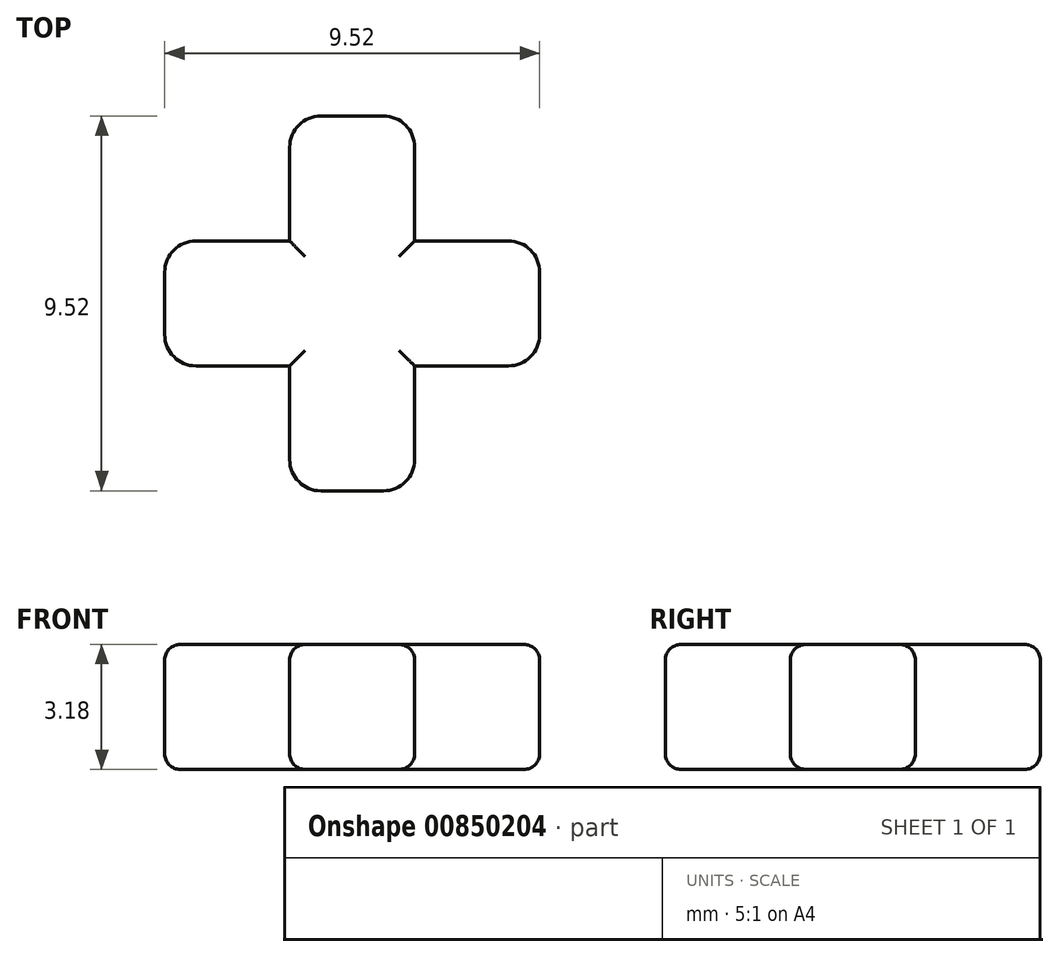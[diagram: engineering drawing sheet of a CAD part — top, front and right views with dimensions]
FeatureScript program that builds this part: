
annotation { "Feature Type Name" : "Feature", "Feature Type Description" : "" }
export const myFeature = defineFeature(function(context is Context, id is Id, definition is map)
    precondition{}
    {
        {
            var Q0;
            Q0=qCreatedBy(makeId("Top.planeOp"),FACE);
            var sketch = newSketch(context, id + "F0", { "sketchPlane" : qUnion([Q0])});
            skLineSegment(sketch, "E0.bottom", {"start": v(0.8, 4.76) * mm, "end": v(-0.8, 4.76) * mm});
            skLineSegment(sketch, "E0.top", {"start": v(0.8, -4.76) * mm, "end": v(-0.8, -4.76) * mm});
            skLineSegment(sketch, "E0.left", {"start": v(1.59, 3.97) * mm, "end": v(1.59, -3.97) * mm});
            skLineSegment(sketch, "E0.right", {"start": v(-1.59, 3.97) * mm, "end": v(-1.59, -3.97) * mm});
            skPoint(sketch, "E0.middle", {"position": v(0, 0) * mm});
            skLineSegment(sketch, "E1.bottom", {"start": v(3.97, 1.59) * mm, "end": v(-3.97, 1.59) * mm});
            skLineSegment(sketch, "E1.top", {"start": v(3.97, -1.59) * mm, "end": v(-3.97, -1.59) * mm});
            skLineSegment(sketch, "E1.left", {"start": v(4.76, 0.8) * mm, "end": v(4.76, -0.8) * mm});
            skLineSegment(sketch, "E1.right", {"start": v(-4.76, 0.8) * mm, "end": v(-4.76, -0.8) * mm});
            skPoint(sketch, "E2.visualSharp", {"position": v(-1.59, 4.76) * mm});
            skArc(sketch, "E2.filletArc", {"start": v(-0.8, 4.76) * mm, "mid": v(-1.36, 4.53) * mm, "end": v(-1.59, 3.97) * mm});
            skPoint(sketch, "E3.visualSharp", {"position": v(1.59, 4.76) * mm});
            skArc(sketch, "E3.filletArc", {"start": v(1.59, 3.97) * mm, "mid": v(1.36, 4.53) * mm, "end": v(0.8, 4.76) * mm});
            skPoint(sketch, "E4.visualSharp", {"position": v(4.76, 1.59) * mm});
            skArc(sketch, "E4.filletArc", {"start": v(4.76, 0.8) * mm, "mid": v(4.53, 1.36) * mm, "end": v(3.97, 1.59) * mm});
            skPoint(sketch, "E5.visualSharp", {"position": v(4.76, -1.59) * mm});
            skArc(sketch, "E5.filletArc", {"start": v(3.97, -1.59) * mm, "mid": v(4.53, -1.36) * mm, "end": v(4.76, -0.8) * mm});
            skPoint(sketch, "E6.visualSharp", {"position": v(1.59, -4.76) * mm});
            skArc(sketch, "E6.filletArc", {"start": v(0.8, -4.76) * mm, "mid": v(1.36, -4.53) * mm, "end": v(1.59, -3.97) * mm});
            skPoint(sketch, "E7.visualSharp", {"position": v(-1.59, -4.76) * mm});
            skArc(sketch, "E7.filletArc", {"start": v(-1.59, -3.97) * mm, "mid": v(-1.36, -4.53) * mm, "end": v(-0.8, -4.76) * mm});
            skPoint(sketch, "E8.visualSharp", {"position": v(-4.76, -1.59) * mm});
            skArc(sketch, "E8.filletArc", {"start": v(-4.76, -0.8) * mm, "mid": v(-4.53, -1.36) * mm, "end": v(-3.97, -1.59) * mm});
            skPoint(sketch, "E9.visualSharp", {"position": v(-4.76, 1.59) * mm});
            skArc(sketch, "E9.filletArc", {"start": v(-3.97, 1.59) * mm, "mid": v(-4.53, 1.36) * mm, "end": v(-4.76, 0.8) * mm});
            skSolve(sketch);
        }
        {
            var Q0;
            Q0 = qSketchRegion(id + "F0", true);
            extrude(context, id + "F1", {"entities" : qUnion([Q0]), "depth" : 3.17 * mm, "offsetDistance" : 25.4 * mm});
        }
        {
            var Q0;
            Q0=makeQuery(id+"F1.opExtrude","CAP_FACE",FACE,{"disambiguationData":[OSD([sQuery(id+"F0.wireOp",EDGE,"E0.bottom"),sQuery(id+"F0.wireOp",EDGE,"E0.top"),sQuery(id+"F0.wireOp",EDGE,"E0.left"),sQuery(id+"F0.wireOp",EDGE,"E0.right"),sQuery(id+"F0.wireOp",EDGE,"E1.bottom"),sQuery(id+"F0.wireOp",EDGE,"E1.top"),sQuery(id+"F0.wireOp",EDGE,"E1.left"),sQuery(id+"F0.wireOp",EDGE,"E1.right"),sQuery(id+"F0.wireOp",EDGE,"E2.filletArc"),sQuery(id+"F0.wireOp",EDGE,"E3.filletArc"),sQuery(id+"F0.wireOp",EDGE,"E4.filletArc"),sQuery(id+"F0.wireOp",EDGE,"E5.filletArc"),sQuery(id+"F0.wireOp",EDGE,"E6.filletArc"),sQuery(id+"F0.wireOp",EDGE,"E7.filletArc"),sQuery(id+"F0.wireOp",EDGE,"E8.filletArc"),sQuery(id+"F0.wireOp",EDGE,"E9.filletArc")])],"isStart":false});
            var Q1;
            Q1=makeQuery(id+"F1.opExtrude","CAP_FACE",FACE,{"disambiguationData":[OSD([sQuery(id+"F0.wireOp",EDGE,"E0.bottom"),sQuery(id+"F0.wireOp",EDGE,"E0.top"),sQuery(id+"F0.wireOp",EDGE,"E0.left"),sQuery(id+"F0.wireOp",EDGE,"E0.right"),sQuery(id+"F0.wireOp",EDGE,"E1.bottom"),sQuery(id+"F0.wireOp",EDGE,"E1.top"),sQuery(id+"F0.wireOp",EDGE,"E1.left"),sQuery(id+"F0.wireOp",EDGE,"E1.right"),sQuery(id+"F0.wireOp",EDGE,"E2.filletArc"),sQuery(id+"F0.wireOp",EDGE,"E3.filletArc"),sQuery(id+"F0.wireOp",EDGE,"E4.filletArc"),sQuery(id+"F0.wireOp",EDGE,"E5.filletArc"),sQuery(id+"F0.wireOp",EDGE,"E6.filletArc"),sQuery(id+"F0.wireOp",EDGE,"E7.filletArc"),sQuery(id+"F0.wireOp",EDGE,"E8.filletArc"),sQuery(id+"F0.wireOp",EDGE,"E9.filletArc")])],"isStart":true});
            fillet(context, id + "F2", {"entities" : qUnion([Q0, Q1]), "tangentPropagation" : true, "radius" : 0.4 * mm, "defaultsChanged" : true, "vertexSettings" : [], "allowEdgeOverflow" : false});
        }
    });
